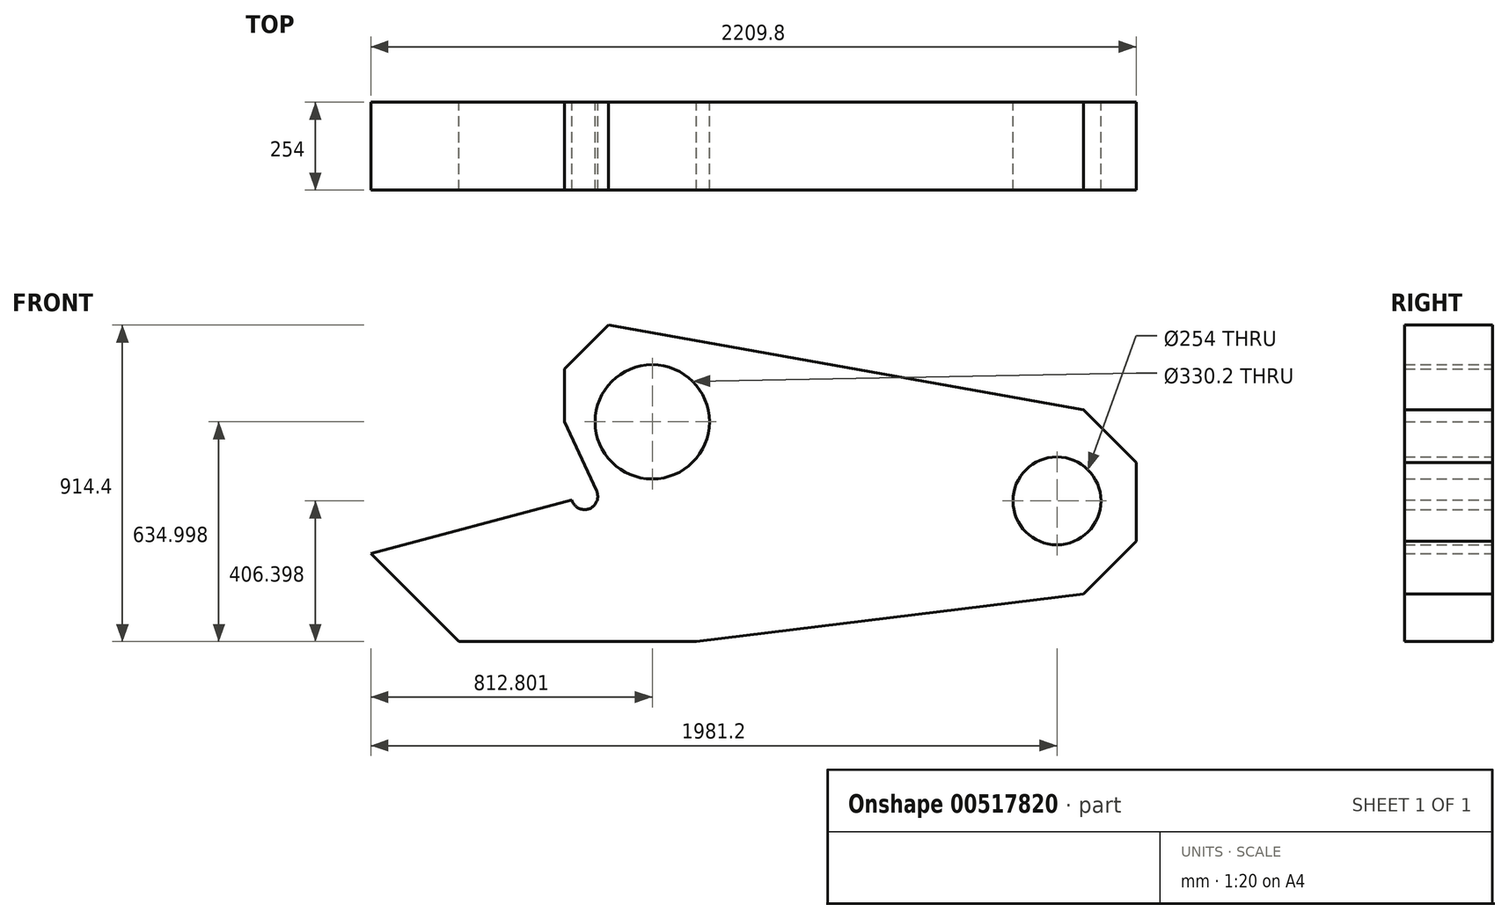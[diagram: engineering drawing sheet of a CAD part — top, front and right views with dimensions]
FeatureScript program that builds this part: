
annotation { "Feature Type Name" : "Feature", "Feature Type Description" : "" }
export const myFeature = defineFeature(function(context is Context, id is Id, definition is map)
    precondition{}
    {
        {
            var Q0;
            Q0=qCreatedBy(makeId("Front.planeOp"),FACE);
            var sketch = newSketch(context, id + "F0", { "sketchPlane" : qUnion([Q0])});
            skLineSegment(sketch, "E0", {"start": v(1466.95, -299.3) * mm, "end": v(1466.95, -71.25) * mm});
            skCircle(sketch, "E1", {"center": v(1238.35, -182.53) * mm, "radius": 127 * mm});
            skLineSegment(sketch, "E2", {"start": v(-184.05, 46.07) * mm, "end": v(-184.05, 198.47) * mm});
            skLineSegment(sketch, "E3", {"start": v(-184.05, 198.47) * mm, "end": v(-57.05, 325.47) * mm});
            skLineSegment(sketch, "E4", {"start": v(196.95, -588.93) * mm, "end": v(1314.55, -451.7) * mm});
            skLineSegment(sketch, "E5", {"start": v(-57.05, 325.47) * mm, "end": v(1314.55, 81.15) * mm});
            skLineSegment(sketch, "E6", {"start": v(1314.55, 81.15) * mm, "end": v(1466.95, -71.25) * mm});
            skLineSegment(sketch, "E7", {"start": v(1314.55, -451.7) * mm, "end": v(1466.95, -299.3) * mm});
            skLineSegment(sketch, "E8", {"start": v(196.95, -588.93) * mm, "end": v(-488.85, -588.93) * mm});
            skLineSegment(sketch, "E9", {"start": v(-162.36, -179.39) * mm, "end": v(-742.85, -334.93) * mm});
            skLineSegment(sketch, "E10", {"start": v(-488.85, -588.93) * mm, "end": v(-742.85, -334.93) * mm});
            skCircle(sketch, "E11", {"center": v(69.95, 46.07) * mm, "radius": 165.1 * mm});
            skLineSegment(sketch, "E12", {"start": v(-184.05, 46.07) * mm, "end": v(-91.02, -153.43) * mm});
            skArc(sketch, "E13", {"start": v(-162.36, -179.39) * mm, "mid": v(-112.52, -205.33) * mm, "end": v(-91.02, -153.43) * mm});
            skSolve(sketch);
        }
        {
            var Q0;
            Q0=makeQuery(id+"F0.imprint","IMPRINT",FACE,{"disambiguationData":[TD([[makeQuery(id+"F0.imprint","IMPRINT",EDGE,{"derivedFrom":sQuery(id+"F0.wireOp",EDGE,"E0")}),1.0]])]});
            extrude(context, id + "F1", {"entities" : qUnion([Q0]), "depth" : 254 * mm, "offsetDistance" : 25.4 * mm});
        }
    });
